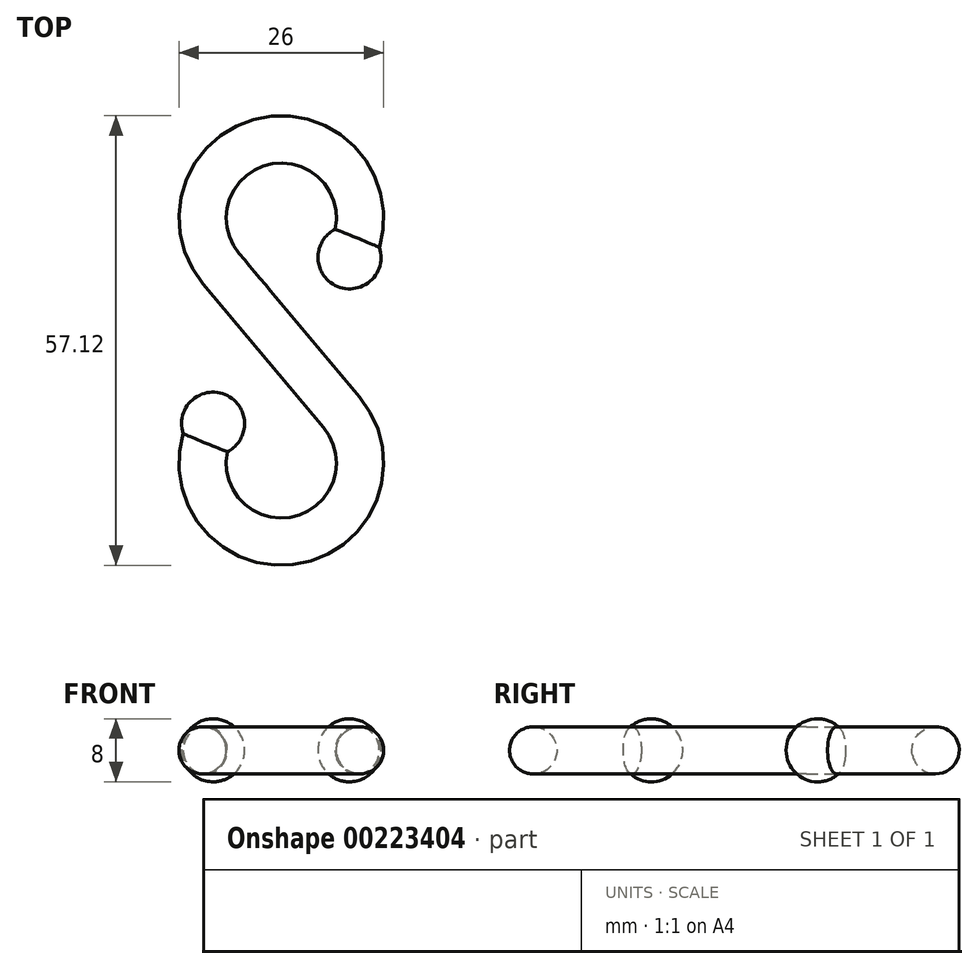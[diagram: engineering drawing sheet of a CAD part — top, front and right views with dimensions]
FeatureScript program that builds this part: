
annotation { "Feature Type Name" : "Feature", "Feature Type Description" : "" }
export const myFeature = defineFeature(function(context is Context, id is Id, definition is map)
    precondition{}
    {
        {
            var Q0;
            Q0=qCreatedBy(makeId("Top.planeOp"),FACE);
            var sketch = newSketch(context, id + "F0", { "sketchPlane" : qUnion([Q0])});
            skLineSegment(sketch, "E0", {"start": v(-7.66, 9.13) * mm, "end": v(0, 0) * mm});
            skLineSegment(sketch, "E1", {"start": v(0, 0) * mm, "end": v(7.66, -9.13) * mm});
            skArc(sketch, "E2", {"start": v(-8.66, -10.56) * mm, "mid": v(0.87, -25.52) * mm, "end": v(7.66, -9.13) * mm});
            skArc(sketch, "E3", {"start": v(8.66, 10.56) * mm, "mid": v(-0.87, 25.52) * mm, "end": v(-7.66, 9.13) * mm});
            skSolve(sketch);
        }
        {
            var Q0;
            Q0=sQuery(id+"F0.wireOp",VERTEX,"E3.start");
            var Q1;
            Q1=sQuery(id+"F0.wireOp",EDGE,"E3");
            cPlane(context, id + "F1", {"entities" : qUnion([Q0, Q1]), "cplaneType" : CPlaneType.CURVE_POINT, "offset" : 25 * mm, "width" : 150 * mm, "height" : 150 * mm});
        }
        {
            var Q0;
            Q0=qCreatedBy(id+"F1.planeOp",FACE);
            var sketch = newSketch(context, id + "F2", { "sketchPlane" : qUnion([Q0])});
            skCircle(sketch, "E4", {"center": v(-2.22, 0) * mm, "radius": 3 * mm});
            skSolve(sketch);
        }
        {
            var Q0;
            Q0 = qSketchRegion(id + "F2", true);
            var Q1;
            Q1 = qConstructionFilter(qBodyType(qCreatedBy(id + "F0" ,EDGE), BodyType.WIRE), ConstructionObject.NO);
            sweep(context, id + "F3", {"profiles" : qUnion([Q0]), "path" : qUnion([Q1])});
        }
        {
            var Q0;
            Q0=makeQuery(id+"F3.opSweep","CAP_FACE",FACE,{"disambiguationData":[OSD([sQuery(id+"F0.wireOp",VERTEX,"E3.start"),sQuery(id+"F2.wireOp",EDGE,"E4")])],"isStart":true});
            var sketch = newSketch(context, id + "F4", { "sketchPlane" : qUnion([Q0])});
            skLineSegment(sketch, "E5", {"start": v(2.22, 4) * mm, "end": v(2.22, -4) * mm});
            skArc(sketch, "E6", {"start": v(2.22, 4) * mm, "mid": v(-1.78, 0) * mm, "end": v(2.22, -4) * mm});
            skSolve(sketch);
        }
        {
            var Q0;
            Q0 = qSketchRegion(id + "F4", true);
            var Q1;
            Q1=sQuery(id+"F4.wireOp",EDGE,"E5");
            revolve(context, id + "F5", {"operationType" : NewBodyOperationType.ADD, "entities" : qUnion([Q0]), "axis" : qUnion([Q1]), "revolveType" : RevolveType.FULL});
        }
        {
            var Q0;
            Q0=makeQuery(id+"F3.opSweep","CAP_FACE",FACE,{"disambiguationData":[OSD([sQuery(id+"F0.wireOp",VERTEX,"E2.start"),sQuery(id+"F2.wireOp",EDGE,"E4")])],"isStart":false});
            var sketch = newSketch(context, id + "F6", { "sketchPlane" : qUnion([Q0])});
            skLineSegment(sketch, "E7", {"start": v(2.04, -2.88) * mm, "end": v(2.47, 3.8) * mm, "construction": true});
            skPoint(sketch, "E8", {"position": v(2.22, 0) * mm});
            skSolve(sketch);
        }
        {
            var Q0;
            Q0=makeQuery(id+"F6.imprint","IMPRINT",FACE,{"disambiguationData":[TD([[makeQuery(id+"F6.imprint","IMPRINT",EDGE,{"derivedFrom":makeQuery(id+"F3.opSweep","CAP_EDGE",EDGE,{"disambiguationData":[OSD([sQuery(id+"F0.wireOp",VERTEX,"E2.start"),sQuery(id+"F2.wireOp",EDGE,"E4")])],"isStart":false})}),1.0]])]});
            var sketch = newSketch(context, id + "F7", { "sketchPlane" : qUnion([Q0])});
            skArc(sketch, "E9", {"start": v(2.48, 4) * mm, "mid": v(-1.77, 0.26) * mm, "end": v(1.96, -4) * mm});
            skLineSegment(sketch, "E10", {"start": v(2.48, 4) * mm, "end": v(1.96, -4) * mm});
            skSolve(sketch);
        }
        {
            var Q0;
            Q0 = qSketchRegion(id + "F7", true);
            var Q1;
            Q1=sQuery(id+"F6.wireOp",EDGE,"E7");
            revolve(context, id + "F8", {"operationType" : NewBodyOperationType.ADD, "entities" : qUnion([Q0]), "axis" : qUnion([Q1]), "revolveType" : RevolveType.FULL});
        }
        {
            var Q0;
            Q0=sQuery(id+"F0.wireOp",VERTEX,"E1.start");
            var Q1;
            Q1=sQuery(id+"F0.wireOp",EDGE,"E1");
            cPlane(context, id + "F9", {"entities" : qUnion([Q0, Q1]), "cplaneType" : CPlaneType.LINE_POINT, "offset" : 25 * mm, "width" : 150 * mm, "height" : 150 * mm});
        }
    });
